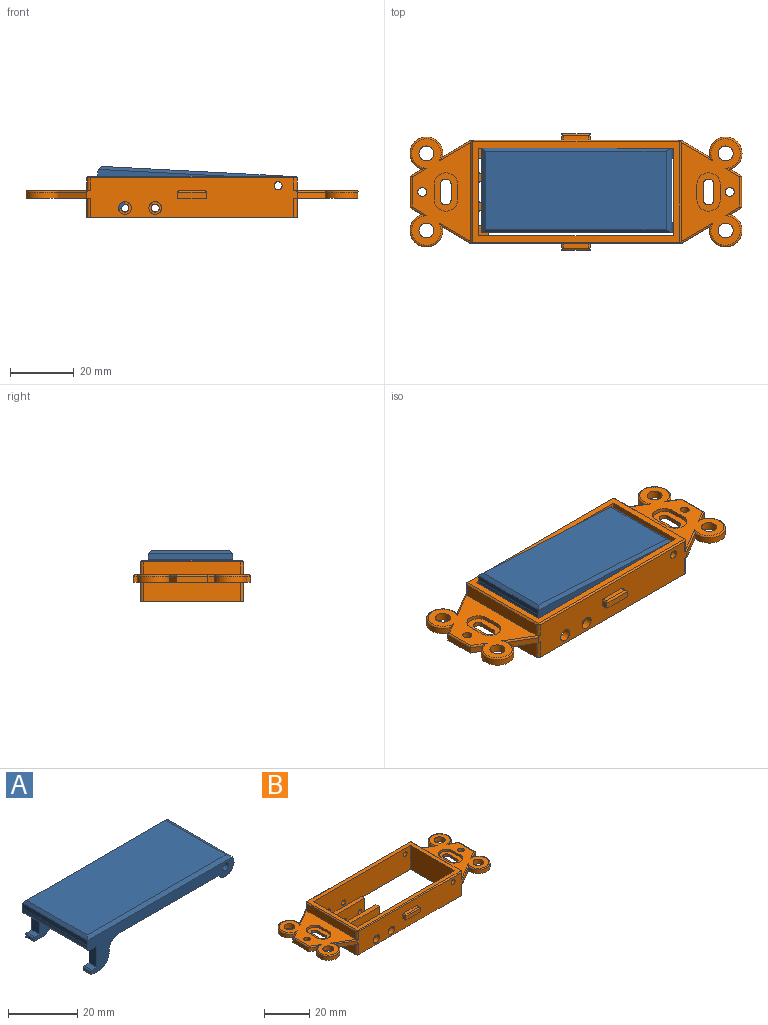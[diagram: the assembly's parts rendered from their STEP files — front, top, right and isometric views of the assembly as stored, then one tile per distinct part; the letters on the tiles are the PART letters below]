
ASSEMBLY  parts=2 mates=1
PART A: 55 faces, bbox 60.1x26.6x14 mm
  f0: plane 60.1x13mm, normal (0,-1,0), area 288.8mm2, adj f2,f10,f11,f12,f14,f16,f18,f19
  f1: plane 60.1x13mm, normal (0,1,0), area 288.8mm2, adj f10,f11,f13,f14,f20,f22,f23,f24
  f2: plane 59.3x1mm, normal (0,-0.71,0.71), area 82.3mm2, adj f0,f15,f23,f25
  f3: plane 19x5.02mm, normal (0,-1,0), area 67mm2, adj f5,f10,f23,f24,f37
  f4: plane 19x5.02mm, normal (0,1,0), area 67mm2, adj f5,f10,f12,f23,f37
  f5: plane 20.3x18.55mm, normal (0,0,-1), area 376.7mm2, adj f3,f4,f23,f37
  f6: cylinder r=3.5mm len=6.97mm, axis (0,0,1), area 30.9mm2, adj f8,f47,f48,f50
  f7: cylinder r=3.5mm len=6.97mm, axis (0,0,1), area 30.9mm2, adj f41,f46,f49,f50
  f8: plane 6.97x3.15mm, normal (0,0,-1), area 10.4mm2, adj f6,f9,f47,f48
  f9: cylinder r=2.25mm len=4.45mm, axis (0,0,-1), area 25.5mm2, adj f8,f43,f47,f48
  f10: plane 40.94x26.6mm, normal (0,0,-1), area 420.7mm2, adj f0,f1,f3,f4,f17,f21,f23,f33
  f11: plane 26.6x2.82mm, normal (0,0,-1), area 22.3mm2, adj f0,f1,f13,f16,f17,f21,f38,f54
  f12: cylinder r=1.25mm len=3.15mm, axis (0,-1,0), area 24.7mm2, adj f0,f4
  f13: plane 7.5x3.15mm, normal (-1,0,0), area 23.6mm2, adj f1,f11,f21,f27
  f14: plane 26.6x1.82mm, normal (-1,0,0), area 48.4mm2, adj f0,f1,f25,f51
  f15: plane 56.83x24.6mm, normal (0,0,1), area 1398.1mm2, adj f2,f23,f25,f26
  f16: plane 7.5x3.15mm, normal (-1,0,0), area 23.6mm2, adj f0,f11,f17,f29
  f17: plane 27x12mm, normal (0,1,0), area 129.6mm2, adj f10,f11,f16,f18,f19,f29,f30,f32
  f18: plane 3.15x1mm, normal (1,0,0), area 3.2mm2, adj f0,f17,f35,f36
  f19: plane 3.15x3mm, normal (0,0,-1), area 9.5mm2, adj f0,f17,f32,f36
  f20: plane 3.15x1mm, normal (1,0,0), area 3.2mm2, adj f1,f21,f33,f34
  f21: plane 27x12mm, normal (0,-1,0), area 129.6mm2, adj f10,f11,f13,f20,f22,f27,f28,f31
  f22: plane 3.15x3mm, normal (0,0,-1), area 9.4mm2, adj f1,f21,f31,f34
  f23: cylinder r=3.35mm len=26.6mm, axis (0,-1,0), area 127.2mm2, adj f0,f1,f2,f3,f4,f5,f10,f15
  f24: cylinder r=1.25mm len=3.15mm, axis (0,-1,0), area 24.7mm2, adj f1,f3
  f25: plane 26.6x1mm, normal (-0.71,0,0.71), area 36.2mm2, adj f2,f14,f15,f26
  f26: plane 59.3x1mm, normal (0,0.71,0.71), area 82.3mm2, adj f1,f15,f23,f25
  f27: plane 3.15x2mm, normal (0,0,1), area 6.3mm2, adj f1,f13,f21,f52
  f28: plane 3.15x0.5mm, normal (-1,0,0), area 1.6mm2, adj f1,f21,f31,f52
  f29: plane 3.15x2mm, normal (0,0,1), area 6.3mm2, adj f0,f16,f17,f53
  f30: plane 3.15x0.5mm, normal (-1,0,0), area 1.6mm2, adj f0,f17,f32,f53
  f31: cylinder r=0.5mm len=3.15mm, axis (0,-1,0), area 2.5mm2, adj f1,f21,f22,f28
  f32: cylinder r=0.5mm len=3.15mm, axis (0,-1,0), area 2.5mm2, adj f0,f17,f19,f30
  f33: cylinder r=4mm len=4mm, axis (0,1,0), area 19.8mm2, adj f1,f10,f20,f21
  f34: cylinder r=4mm len=4mm, axis (0,1,0), area 19.8mm2, adj f1,f20,f21,f22
  f35: cylinder r=4mm len=4mm, axis (0,1,0), area 19.8mm2, adj f0,f10,f17,f18
  f36: cylinder r=4mm len=4mm, axis (0,1,0), area 19.8mm2, adj f0,f17,f18,f19
  f37: plane 20.3x3.5mm, normal (1,0,0), area 71.1mm2, adj f3,f4,f5,f10
  f38: plane 20.3x3mm, normal (1,0,0), area 60.9mm2, adj f11,f17,f21,f40
  f39: plane 20.3x3mm, normal (-1,0,0), area 60.9mm2, adj f10,f17,f21,f40
  f40: plane 27x20.3mm, normal (0,0,-1), area 548.1mm2, adj f17,f21,f38,f39
  f41: plane 6.97x3.15mm, normal (0,0,-1), area 10.4mm2, adj f7,f42,f46,f49
  f42: cylinder r=2.25mm len=4.45mm, axis (0,0,-1), area 25.5mm2, adj f41,f43,f46,f49
  f43: plane 7.54x4.5mm, normal (0,0,-1), area 9.5mm2, adj f9,f42,f44,f46,f47,f48,f49,f50
  f44: cylinder r=1.65mm len=5mm, axis (0,0,-1), area 51.8mm2, adj f43,f45
  f45: plane 3.3x3.3mm, normal (0,0,-1), area 8.6mm2, adj f44
  f46: plane 4.01x1.54mm, normal (0,1,0), area 5.1mm2, adj f7,f41,f42,f43,f50
  f47: plane 4.01x1.54mm, normal (0,-1,0), area 5.1mm2, adj f6,f8,f9,f43,f50
  f48: plane 4.01x1.54mm, normal (0,-1,0), area 5.1mm2, adj f6,f8,f9,f43,f50
  f49: plane 4.01x1.54mm, normal (0,1,0), area 5.1mm2, adj f7,f41,f42,f43,f50
  f50: torus R=5.5mm, axis (0,0,1), area 82mm2, adj f6,f7,f10,f43,f46,f47,f48,f49
  f51: cylinder r=5mm len=26.6mm, axis (0,-1,0), area 39.8mm2, adj f0,f1,f14,f54
  f52: cylinder r=0.5mm len=3.15mm, axis (0,-1,0), area 2.5mm2, adj f1,f21,f27,f28
  f53: cylinder r=0.5mm len=3.15mm, axis (0,-1,0), area 2.5mm2, adj f0,f17,f29,f30
  f54: cylinder r=1mm len=26.6mm, axis (0,-1,0), area 33.8mm2, adj f0,f1,f11,f51
PART B: 126 faces, bbox 105.1x36.5x13 mm
  f0: cylinder r=1.65mm len=3.3mm, axis (0,0,1), area 6.7mm2, adj f1,f3,f64,f97
  f1: plane 4.83x1.3mm, normal (-1,0,0), area 6.3mm2, adj f0,f2,f64,f97
  f2: cylinder r=1.65mm len=3.3mm, axis (0,0,1), area 6.7mm2, adj f1,f3,f64,f97
  f3: plane 4.83x1.3mm, normal (1,0,0), area 6.3mm2, adj f0,f2,f64,f97
  f4: cylinder r=1.65mm len=3.3mm, axis (0,0,1), area 6.7mm2, adj f5,f7,f76,f92
  f5: plane 4.83x1.3mm, normal (1,0,0), area 6.3mm2, adj f4,f6,f76,f92
  f6: cylinder r=1.65mm len=3.3mm, axis (0,0,1), area 6.7mm2, adj f5,f7,f76,f92
  f7: plane 4.83x1.3mm, normal (-1,0,0), area 6.3mm2, adj f4,f6,f76,f92
  f8: plane 30.5x4mm, normal (-1,0,0), area 122mm2, adj f20,f77,f122,f123
  f9: plane 30.5x6mm, normal (1,0,0), area 183mm2, adj f12,f64,f120,f121
  f10: plane 61.1x13mm, normal (0,-1,0), area 768mm2, adj f11,f12,f18,f19,f28,f30,f31,f44
  f11: plane 65x31.5mm, normal (0,0,1), area 361.1mm2, adj f10,f17,f18,f19,f20,f21,f22,f23
  f12: plane 66x32.5mm, normal (0,0,-1), area 551mm2, adj f9,f10,f14,f15,f16,f17,f18,f19
  f13: plane 30.5x4mm, normal (1,0,0), area 122mm2, adj f23,f65,f124,f125
  f14: plane 66x12.5mm, normal (0,1,0), area 767.7mm2, adj f12,f21,f44,f45,f53,f55,f64,f73
  f15: plane 30.5x6mm, normal (-1,0,0), area 183mm2, adj f12,f76,f118,f119
  f16: plane 66x12.5mm, normal (0,-1,0), area 752.4mm2, adj f12,f22,f46,f47,f52,f56,f64,f71
  f17: plane 61.1x13mm, normal (0,1,0), area 752.7mm2, adj f11,f12,f18,f19,f24,f25,f27,f46
  f18: plane 27.6x13mm, normal (-1,0,0), area 358.8mm2, adj f10,f11,f12,f17
  f19: plane 27.6x13mm, normal (1,0,0), area 260.7mm2, adj f10,f11,f12,f17,f24,f25,f26,f28
  f20: plane 31.91x0.5mm, normal (-0.71,0,0.71), area 22.3mm2, adj f8,f11,f21,f22,f122,f123
  f21: plane 65.41x0.5mm, normal (0,0.71,0.71), area 46mm2, adj f11,f14,f20,f23,f123,f125
  f22: plane 65.41x0.5mm, normal (0,-0.71,0.71), area 46mm2, adj f11,f16,f20,f23,f122,f124
  f23: plane 31.91x0.5mm, normal (0.71,0,0.71), area 22.3mm2, adj f11,f13,f21,f22,f124,f125
  f24: plane 3.15x3mm, normal (0,0,1), area 9.5mm2, adj f17,f19,f26,f27
  f25: plane 3.15x3mm, normal (0,0,-1), area 9.5mm2, adj f17,f19,f26,f27
  f26: plane 3.85x3mm, normal (0,1,0), area 11.5mm2, adj f19,f24,f25,f27
  f27: plane 3.85x3.15mm, normal (1,0,0), area 12.1mm2, adj f17,f24,f25,f26
  f28: plane 3.15x3mm, normal (0,0,1), area 9.4mm2, adj f10,f19,f29,f31
  f29: plane 3.85x3mm, normal (0,-1,0), area 11.5mm2, adj f19,f28,f30,f31
  f30: plane 3.15x3mm, normal (0,0,-1), area 9.5mm2, adj f10,f19,f29,f31
  f31: plane 3.85x3.15mm, normal (1,0,0), area 12.1mm2, adj f10,f28,f29,f30
  f32: plane 22x4.1mm, normal (0,0,1), area 46.6mm2, adj f19,f33,f34,f35,f50,f51
  f33: plane 21x9mm, normal (0,-1,0), area 179.2mm2, adj f12,f32,f35,f42,f43,f50
  f34: plane 21x9mm, normal (0,1,0), area 179.2mm2, adj f12,f32,f35,f42,f43,f51
  f35: plane 9x2.1mm, normal (1,0,0), area 18.9mm2, adj f12,f32,f33,f34
  f36: plane 22x4.1mm, normal (0,0,1), area 46.6mm2, adj f19,f37,f38,f39,f48,f49
  f37: plane 21x9mm, normal (0,-1,0), area 179.2mm2, adj f12,f36,f39,f40,f41,f48
  f38: plane 21x9mm, normal (0,1,0), area 179.2mm2, adj f12,f36,f39,f40,f41,f49
  f39: plane 9x2.1mm, normal (1,0,0), area 18.9mm2, adj f12,f36,f37,f38
  f40: cylinder r=1.25mm len=2.5mm, axis (0,-1,0), area 16.5mm2, adj f37,f38
  f41: cylinder r=1.25mm len=2.5mm, axis (0,-1,0), area 16.5mm2, adj f37,f38
  f42: cylinder r=1.25mm len=2.5mm, axis (0,-1,0), area 16.5mm2, adj f33,f34
  f43: cylinder r=1.25mm len=2.5mm, axis (0,-1,0), area 16.5mm2, adj f33,f34
  f44: cylinder r=1.25mm len=2.5mm, axis (0,-1,0), area 19.2mm2, adj f10,f14
  f45: cylinder r=1.25mm len=2.5mm, axis (0,-1,0), area 19.2mm2, adj f10,f14
  f46: cylinder r=2mm len=4mm, axis (0,-1,0), area 30.8mm2, adj f16,f17
  f47: cylinder r=2mm len=4mm, axis (0,-1,0), area 30.8mm2, adj f16,f17
  f48: cylinder r=1mm len=9mm, axis (0,0,1), area 14.1mm2, adj f12,f19,f36,f37
  f49: cylinder r=1mm len=9mm, axis (0,0,-1), area 14.1mm2, adj f12,f19,f36,f38
  f50: cylinder r=1mm len=9mm, axis (0,0,1), area 14.1mm2, adj f12,f19,f32,f33
  f51: cylinder r=1mm len=9mm, axis (0,0,-1), area 14.1mm2, adj f12,f19,f32,f34
  f52: cylinder r=1.25mm len=2.5mm, axis (0,-1,0), area 19.2mm2, adj f16,f17
  f53: cylinder r=1.25mm len=2.5mm, axis (0,-1,0), area 19.2mm2, adj f10,f14
  f54: cylinder r=5.15mm len=10.3mm, axis (0,0,1), area 48.1mm2, adj f55,f61,f64,f111
  f55: plane 8.98x5.32mm, normal (0.51,0.86,0), area 20.9mm2, adj f14,f54,f64,f110
  f56: plane 8.98x5.32mm, normal (0.51,-0.86,0), area 20.9mm2, adj f16,f57,f64,f105
  f57: cylinder r=5.15mm len=10.3mm, axis (0,0,1), area 48.1mm2, adj f56,f58,f64,f106
  f58: plane 3.61x2.14mm, normal (0.51,-0.86,0), area 8.4mm2, adj f57,f59,f64,f107
  f59: plane 10x2mm, normal (1,0,0), area 20mm2, adj f58,f61,f64,f108
  f60: cylinder r=1.4mm len=2.8mm, axis (0,0,1), area 22mm2, adj f64,f65
  f61: plane 3.61x2.14mm, normal (0.51,0.86,0), area 8.4mm2, adj f54,f59,f64,f109
  f62: cylinder r=2.35mm len=4.7mm, axis (0,0,1), area 36.9mm2, adj f64,f65
  f63: cylinder r=2.35mm len=4.7mm, axis (0,0,1), area 36.9mm2, adj f64,f65
  f64: plane 34.5x20.15mm, normal (0,0,-1), area 489.2mm2, adj f0,f1,f2,f3,f9,f14,f16,f54
  f65: plane 33.5x18.78mm, normal (0,0,1), area 391.4mm2, adj f13,f60,f62,f63,f93,f94,f95,f96
  f66: cylinder r=5.15mm len=10.3mm, axis (0,0,1), area 48.1mm2, adj f67,f73,f76,f104
  f67: plane 3.61x2.14mm, normal (-0.51,0.86,0), area 8.4mm2, adj f66,f68,f76,f103
  f68: plane 10x2mm, normal (-1,0,0), area 20mm2, adj f67,f69,f76,f101
  f69: plane 3.61x2.14mm, normal (-0.51,-0.86,0), area 8.4mm2, adj f68,f70,f76,f100
  f70: cylinder r=5.15mm len=10.3mm, axis (0,0,1), area 48.1mm2, adj f69,f71,f76,f99
  f71: plane 8.98x5.32mm, normal (-0.51,-0.86,0), area 20.9mm2, adj f16,f70,f76,f98
  f72: cylinder r=1.4mm len=2.8mm, axis (0,0,1), area 22mm2, adj f76,f77
  f73: plane 8.98x5.32mm, normal (-0.51,0.86,0), area 20.9mm2, adj f14,f66,f76,f102
  f74: cylinder r=2.35mm len=4.7mm, axis (0,0,1), area 36.9mm2, adj f76,f77
  f75: cylinder r=2.35mm len=4.7mm, axis (0,0,1), area 36.9mm2, adj f76,f77
  f76: plane 34.5x20.15mm, normal (0,0,-1), area 489.2mm2, adj f4,f5,f6,f7,f14,f15,f16,f66
  f77: plane 33.5x18.78mm, normal (0,0,1), area 391.4mm2, adj f8,f72,f74,f75,f88,f89,f90,f91
  f78: plane 2x2mm, normal (-1,0,0), area 4mm2, adj f16,f79,f81,f117
  f79: plane 9x2mm, normal (0,-1,0), area 18mm2, adj f78,f80,f81,f116
  f80: plane 2x2mm, normal (1,0,0), area 4mm2, adj f16,f79,f81,f115
  f81: plane 9x2mm, normal (0,0,-1), area 18mm2, adj f16,f78,f79,f80
  f82: plane 8x1.5mm, normal (0,0,1), area 12mm2, adj f16,f115,f116,f117
  f83: plane 2x2mm, normal (-1,0,0), area 4mm2, adj f14,f85,f86,f112
  f84: plane 2x2mm, normal (1,0,0), area 4mm2, adj f14,f85,f86,f114
  f85: plane 9x2mm, normal (0,1,0), area 18mm2, adj f83,f84,f86,f113
  f86: plane 9x2mm, normal (0,0,-1), area 18mm2, adj f14,f83,f84,f85
  f87: plane 8x1.5mm, normal (0,0,1), area 12mm2, adj f14,f112,f113,f114
  f88: plane 4.83x1.2mm, normal (-1,0,0), area 5.8mm2, adj f77,f89,f91,f92
  f89: cylinder r=3.65mm len=7.3mm, axis (0,0,1), area 13.8mm2, adj f77,f88,f90,f92
  f90: plane 4.83x1.2mm, normal (1,0,0), area 5.8mm2, adj f77,f89,f91,f92
  f91: cylinder r=3.65mm len=7.3mm, axis (0,0,1), area 13.8mm2, adj f77,f88,f90,f92
  f92: plane 12.13x7.3mm, normal (0,0,1), area 52.6mm2, adj f4,f5,f6,f7,f88,f89,f90,f91
  f93: cylinder r=3.65mm len=7.3mm, axis (0,0,1), area 13.8mm2, adj f65,f94,f96,f97
  f94: plane 4.83x1.2mm, normal (-1,0,0), area 5.8mm2, adj f65,f93,f95,f97
  f95: cylinder r=3.65mm len=7.3mm, axis (0,0,1), area 13.8mm2, adj f65,f94,f96,f97
  f96: plane 4.83x1.2mm, normal (1,0,0), area 5.8mm2, adj f65,f93,f95,f97
  f97: plane 12.13x7.3mm, normal (0,0,1), area 52.6mm2, adj f0,f1,f2,f3,f93,f94,f95,f96
  f98: cylinder r=0.5mm len=11.24mm, axis (0.86,-0.51,0), area 8.7mm2, adj f16,f71,f77,f99,f122
  f99: torus R=4.65mm, axis (0,0,1), area 19mm2, adj f70,f77,f98,f100
  f100: cylinder r=0.5mm len=5.12mm, axis (0.86,-0.51,0), area 3.6mm2, adj f69,f77,f99,f101
  f101: cylinder r=0.5mm len=10mm, axis (0,-1,0), area 7.7mm2, adj f68,f77,f100,f103
  f102: cylinder r=0.5mm len=11.24mm, axis (-0.86,-0.51,0), area 8.7mm2, adj f14,f73,f77,f104,f123
  f103: cylinder r=0.5mm len=5.12mm, axis (-0.86,-0.51,0), area 3.6mm2, adj f67,f77,f101,f104
  f104: torus R=4.65mm, axis (0,0,1), area 19mm2, adj f66,f77,f102,f103
  f105: cylinder r=0.5mm len=11.24mm, axis (0.86,0.51,0), area 8.7mm2, adj f16,f56,f65,f106,f124
  f106: torus R=4.65mm, axis (0,0,1), area 19mm2, adj f57,f65,f105,f107
  f107: cylinder r=0.5mm len=5.12mm, axis (0.86,0.51,0), area 3.6mm2, adj f58,f65,f106,f108
  f108: cylinder r=0.5mm len=10mm, axis (0,1,0), area 7.7mm2, adj f59,f65,f107,f109
  f109: cylinder r=0.5mm len=5.12mm, axis (-0.86,0.51,0), area 3.6mm2, adj f61,f65,f108,f111
  f110: cylinder r=0.5mm len=11.24mm, axis (-0.86,0.51,0), area 8.7mm2, adj f14,f55,f65,f111,f125
  f111: torus R=4.65mm, axis (0,0,1), area 19mm2, adj f54,f65,f109,f110
  f112: cylinder r=0.5mm len=2mm, axis (0,-1,0), area 1.4mm2, adj f14,f83,f87,f113
  f113: cylinder r=0.5mm len=9mm, axis (-1,0,0), area 6.8mm2, adj f85,f87,f112,f114
  f114: cylinder r=0.5mm len=2mm, axis (0,1,0), area 1.4mm2, adj f14,f84,f87,f113
  f115: cylinder r=0.5mm len=2mm, axis (0,1,0), area 1.4mm2, adj f16,f80,f82,f116
  f116: cylinder r=0.5mm len=9mm, axis (1,0,0), area 6.8mm2, adj f79,f82,f115,f117
  f117: cylinder r=0.5mm len=2mm, axis (0,-1,0), area 1.4mm2, adj f16,f78,f82,f116
  f118: cylinder r=1mm len=6mm, axis (0,0,-1), area 9.4mm2, adj f12,f14,f15,f76
  f119: cylinder r=1mm len=6mm, axis (0,0,1), area 9.4mm2, adj f12,f15,f16,f76
  f120: cylinder r=1mm len=6mm, axis (0,0,-1), area 9.4mm2, adj f9,f12,f16,f64
  f121: cylinder r=1mm len=6mm, axis (0,0,1), area 9.4mm2, adj f9,f12,f14,f64
  f122: cylinder r=1mm len=4.29mm, axis (0,0,1), area 6.4mm2, adj f8,f16,f20,f22,f77,f98
  f123: cylinder r=1mm len=4.29mm, axis (0,0,-1), area 6.4mm2, adj f8,f14,f20,f21,f77,f102
  f124: cylinder r=1mm len=4.29mm, axis (0,0,-1), area 6.4mm2, adj f13,f16,f22,f23,f65,f105
  f125: cylinder r=1mm len=4.29mm, axis (0,0,1), area 6.4mm2, adj f13,f14,f21,f23,f65,f110
PLACE A rot(axis=(0,1,0),3deg) t=(-25.08,-0.56,-17.15)mm
PLACE B t=(-23.43,-1.06,9.5)mm
MATE revolute B.f52 <-> A.f12  axis (0,-1,0) through (36.62,28.99,19.5)mm
